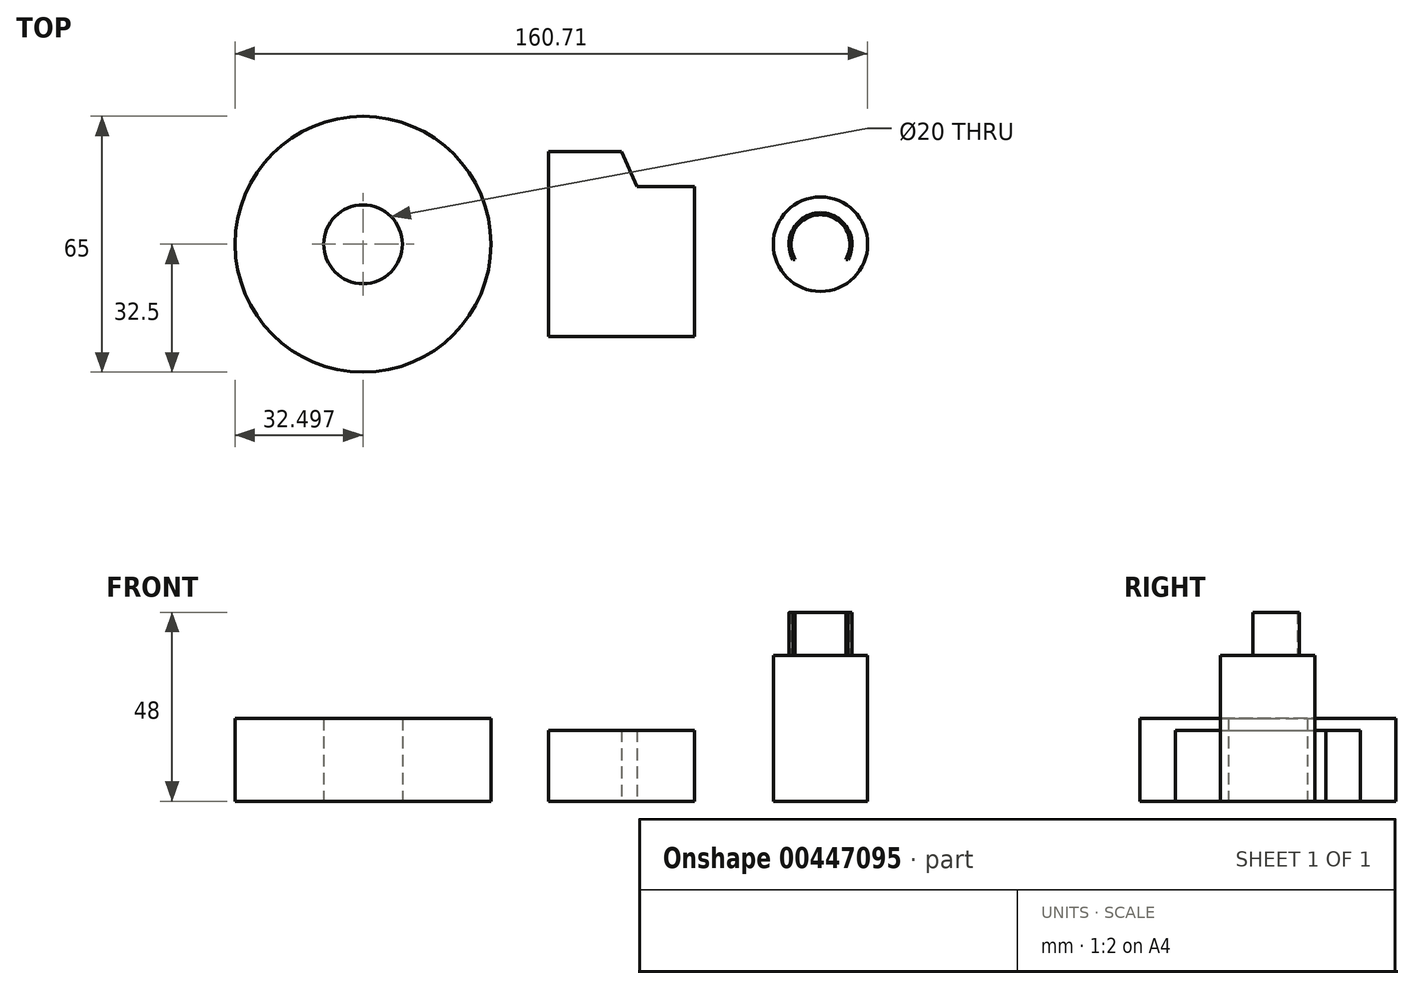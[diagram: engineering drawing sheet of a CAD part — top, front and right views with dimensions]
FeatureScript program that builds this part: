
annotation { "Feature Type Name" : "Feature", "Feature Type Description" : "" }
export const myFeature = defineFeature(function(context is Context, id is Id, definition is map)
    precondition{}
    {
        {
            var Q0;
            Q0=qCreatedBy(makeId("Top.planeOp"),FACE);
            var sketch = newSketch(context, id + "F0", { "sketchPlane" : qUnion([Q0])});
            skCircle(sketch, "E0", {"center": v(-44.24, 0) * mm, "radius": 32.5 * mm});
            skLineSegment(sketch, "E1.bottom", {"start": v(39.92, -23.5) * mm, "end": v(2.92, -23.5) * mm});
            skLineSegment(sketch, "E1.top", {"start": v(21.42, 23.5) * mm, "end": v(2.92, 23.5) * mm});
            skLineSegment(sketch, "E1.left", {"start": v(39.92, -23.5) * mm, "end": v(39.92, 14.69) * mm});
            skLineSegment(sketch, "E1.right", {"start": v(2.92, -23.5) * mm, "end": v(2.92, 23.5) * mm});
            skPoint(sketch, "E1.middle", {"position": v(21.42, 0) * mm});
            skCircle(sketch, "E2", {"center": v(71.97, 0) * mm, "radius": 12 * mm});
            skArc(sketch, "E3", {"start": v(79, -3.84) * mm, "mid": v(71.97, 8) * mm, "end": v(64.96, -3.84) * mm});
            skArc(sketch, "E4", {"start": v(78.42, -3.84) * mm, "mid": v(71.97, 7.5) * mm, "end": v(65.53, -3.84) * mm});
            skLineSegment(sketch, "E5", {"start": v(64.96, -3.84) * mm, "end": v(65.53, -3.84) * mm});
            skLineSegment(sketch, "E6", {"start": v(78.42, -3.84) * mm, "end": v(79, -3.84) * mm});
            skCircle(sketch, "E7", {"center": v(-44.24, 0) * mm, "radius": 10 * mm});
            skLineSegment(sketch, "E8", {"start": v(21.42, 23.5) * mm, "end": v(25.4, 14.69) * mm});
            skLineSegment(sketch, "E9", {"start": v(25.4, 14.69) * mm, "end": v(39.92, 14.69) * mm});
            skPoint(sketch, "E10.orphan", {"position": v(39.92, 23.5) * mm});
            skSolve(sketch);
        }
        {
            var Q0;
            Q0=makeQuery(id+"F0.imprint","IMPRINT",FACE,{"disambiguationData":[TD([[makeQuery(id+"F0.imprint","IMPRINT",EDGE,{"derivedFrom":sQuery(id+"F0.wireOp",EDGE,"E0")}),1.0]])]});
            extrude(context, id + "F1", {"entities" : qUnion([Q0]), "depth" : 21 * mm});
        }
        {
            var Q0;
            Q0=makeQuery(id+"F0.imprint","IMPRINT",FACE,{"disambiguationData":[TD([[makeQuery(id+"F0.imprint","IMPRINT",EDGE,{"derivedFrom":sQuery(id+"F0.wireOp",EDGE,"E1.bottom")}),-1.0]])]});
            extrude(context, id + "F2", {"entities" : qUnion([Q0]), "depth" : 18 * mm});
        }
        {
            var Q0;
            Q0=makeQuery(id+"F0.imprint","IMPRINT",FACE,{"disambiguationData":[TD([[makeQuery(id+"F0.imprint","IMPRINT",EDGE,{"derivedFrom":sQuery(id+"F0.wireOp",EDGE,"E2")}),1.0]])]});
            extrude(context, id + "F3", {"entities" : qUnion([Q0]), "depth" : 37 * mm});
        }
        {
            var Q0;
            Q0=makeQuery(id+"F0.imprint","IMPRINT",FACE,{"disambiguationData":[TD([[makeQuery(id+"F0.imprint","IMPRINT",EDGE,{"derivedFrom":sQuery(id+"F0.wireOp",EDGE,"E3")}),1.0]])]});
            extrude(context, id + "F4", {"entities" : qUnion([Q0]), "operationType" : NewBodyOperationType.ADD, "depth" : 48 * mm});
        }
    });
